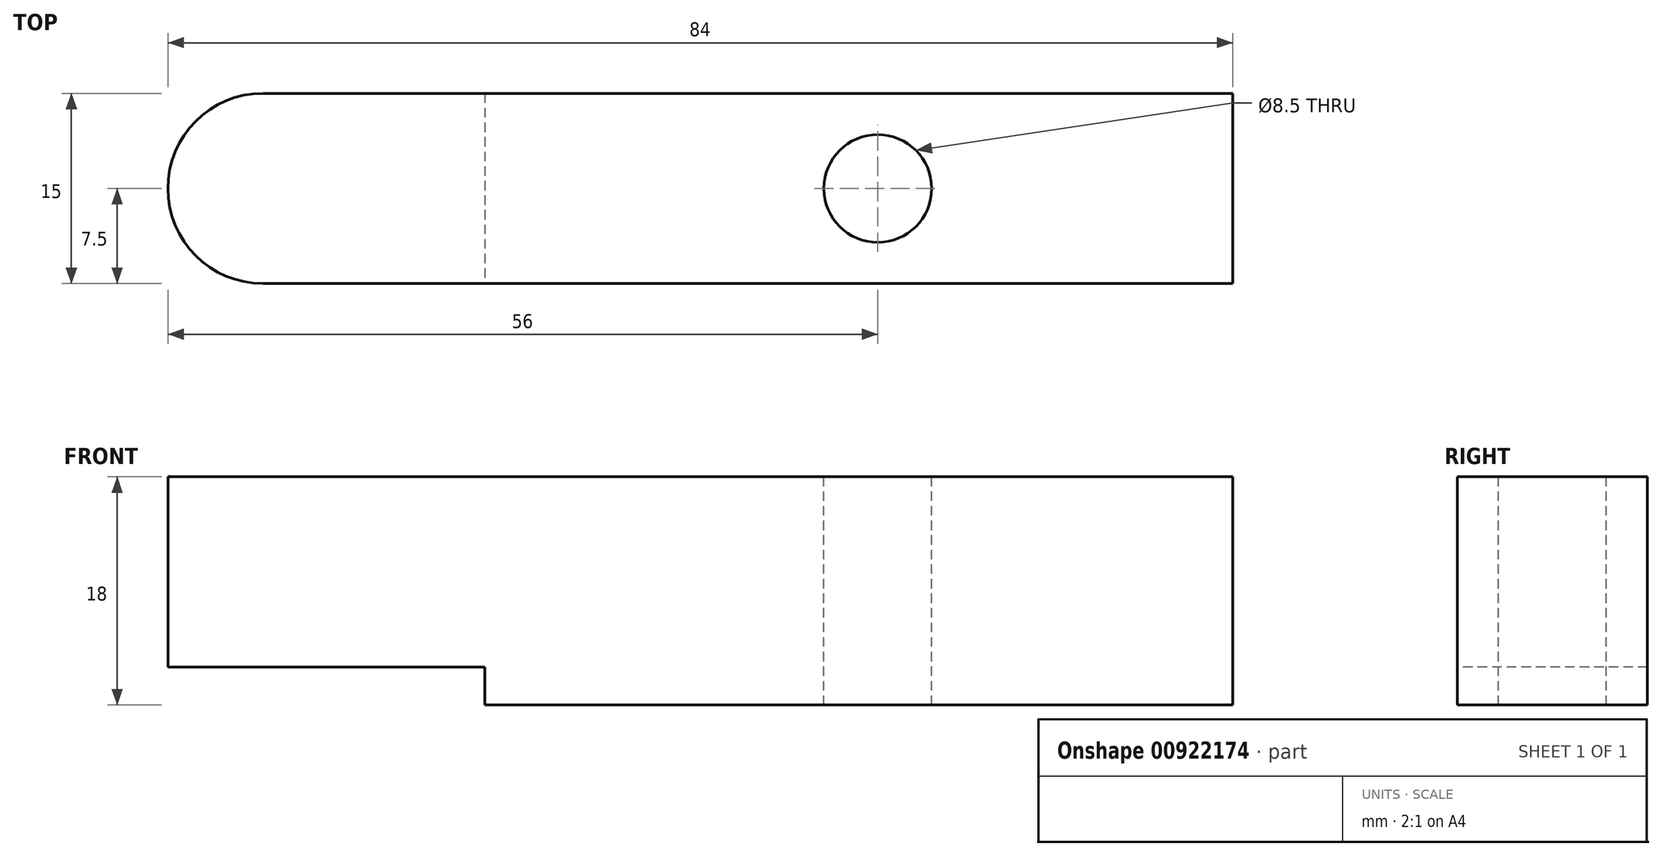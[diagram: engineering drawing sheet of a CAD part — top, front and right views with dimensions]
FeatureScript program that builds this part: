
annotation { "Feature Type Name" : "Feature", "Feature Type Description" : "" }
export const myFeature = defineFeature(function(context is Context, id is Id, definition is map)
    precondition{}
    {
        {
            var Q0;
            Q0=qCreatedBy(makeId("Front.planeOp"),FACE);
            var sketch = newSketch(context, id + "F0", { "sketchPlane" : qUnion([Q0])});
            skLineSegment(sketch, "E0.bottom", {"start": v(42, -7.5) * mm, "end": v(-42, -7.5) * mm});
            skLineSegment(sketch, "E0.top", {"start": v(42, 7.5) * mm, "end": v(-42, 7.5) * mm});
            skLineSegment(sketch, "E0.left", {"start": v(42, -7.5) * mm, "end": v(42, 7.5) * mm});
            skLineSegment(sketch, "E0.right", {"start": v(-42, -7.5) * mm, "end": v(-42, 7.5) * mm});
            skPoint(sketch, "E0.middle", {"position": v(0, 0) * mm});
            skSolve(sketch);
        }
        {
            var Q0;
            Q0 = qSketchRegion(id + "F0", true);
            extrude(context, id + "F1", {"entities" : qUnion([Q0]), "oppositeDirection" : true, "depth" : 15 * mm, "offsetDistance" : 25 * mm});
        }
        {
            var Q0;
            Q0=makeQuery(id+"F1.opExtrude","SWEPT_FACE",FACE,{"disambiguationData":[OSD([sQuery(id+"F0.wireOp",EDGE,"E0.top")])]});
            var sketch = newSketch(context, id + "F2", { "sketchPlane" : qUnion([Q0])});
            skCircle(sketch, "E1", {"center": v(14, 7.5) * mm, "radius": 4.25 * mm});
            skLineSegment(sketch, "E2", {"start": v(-42, 7.5) * mm, "end": v(42, 7.5) * mm, "construction": true});
            skSolve(sketch);
        }
        {
            var Q0;
            Q0=makeQuery(id+"F1.opExtrude","CAP_EDGE",EDGE,{"disambiguationData":[OSD([sQuery(id+"F0.wireOp",EDGE,"E0.right")])],"isStart":false});
            var Q1;
            Q1=makeQuery(id+"F1.opExtrude","CAP_EDGE",EDGE,{"disambiguationData":[OSD([sQuery(id+"F0.wireOp",EDGE,"E0.right")])],"isStart":true});
            fillet(context, id + "F3", {"entities" : qUnion([Q0, Q1]), "radius" : 7.5 * mm, "tangentPropagation" : true, "allowEdgeOverflow" : false});
        }
        {
            var Q0;
            Q0=makeQuery(id+"F1.opExtrude","SWEPT_FACE",FACE,{"disambiguationData":[OSD([sQuery(id+"F0.wireOp",EDGE,"E0.bottom")])]});
            var sketch = newSketch(context, id + "F4", { "sketchPlane" : qUnion([Q0])});
            skLineSegment(sketch, "E3.bottom", {"start": v(42, -15) * mm, "end": v(-17, -15) * mm});
            skLineSegment(sketch, "E3.top", {"start": v(42, 0) * mm, "end": v(-17, 0) * mm});
            skLineSegment(sketch, "E3.left", {"start": v(42, -15) * mm, "end": v(42, 0) * mm});
            skLineSegment(sketch, "E3.right", {"start": v(-17, -15) * mm, "end": v(-17, 0) * mm});
            skPoint(sketch, "E3.middle", {"position": v(12.5, -7.5) * mm});
            skSolve(sketch);
        }
        {
            var Q0;
            Q0 = qSketchRegion(id + "F4", true);
            extrude(context, id + "F5", {"entities" : qUnion([Q0]), "operationType" : NewBodyOperationType.ADD, "depth" : 3 * mm, "offsetDistance" : 25 * mm});
        }
        {
            var Q0;
            Q0=makeQuery(id+"F2.imprint","IMPRINT",FACE,{"disambiguationData":[TD([[makeQuery(id+"F2.imprint","IMPRINT",EDGE,{"derivedFrom":sQuery(id+"F2.wireOp",EDGE,"E1")}),1.0]])]});
            extrude(context, id + "F6", {"entities" : qUnion([Q0]), "operationType" : NewBodyOperationType.REMOVE, "endBound" : BoundingType.THROUGH_ALL, "oppositeDirection" : true, "depth" : 25 * mm, "offsetDistance" : 25 * mm});
        }
    });
